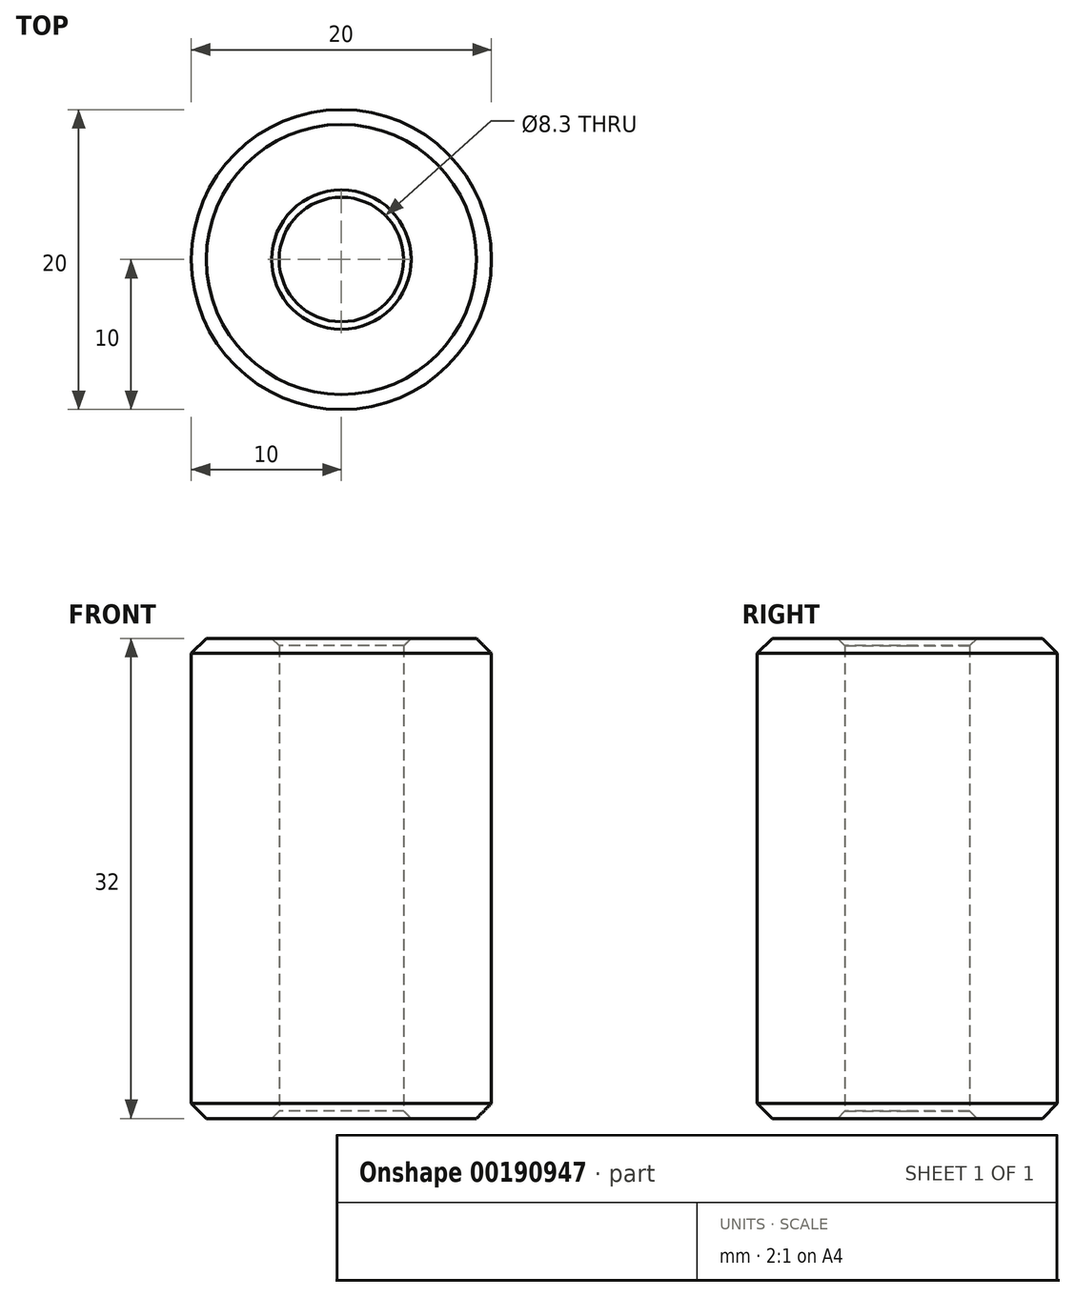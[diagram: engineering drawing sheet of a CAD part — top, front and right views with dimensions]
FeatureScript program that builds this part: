
annotation { "Feature Type Name" : "Feature", "Feature Type Description" : "" }
export const myFeature = defineFeature(function(context is Context, id is Id, definition is map)
    precondition{}
    {
        {
            var Q0;
            Q0=qCreatedBy(makeId("Top.planeOp"),FACE);
            var sketch = newSketch(context, id + "F0", { "sketchPlane" : qUnion([Q0])});
            skCircle(sketch, "E0", {"center": v(0, 0) * mm, "radius": 10 * mm});
            skCircle(sketch, "E1", {"center": v(0, 0) * mm, "radius": 4.15 * mm});
            skSolve(sketch);
        }
        {
            var Q0;
            Q0=makeQuery(id+"F0.imprint","IMPRINT",FACE,{"disambiguationData":[TD([[makeQuery(id+"F0.imprint","IMPRINT",EDGE,{"derivedFrom":sQuery(id+"F0.wireOp",EDGE,"E0")}),1.0]])]});
            extrude(context, id + "F1", {"entities" : qUnion([Q0]), "depth" : 32 * mm});
        }
        {
            var Q0;
            Q0=makeQuery(id+"F1.opExtrude","CAP_EDGE",EDGE,{"disambiguationData":[OSD([sQuery(id+"F0.wireOp",EDGE,"E0")])],"isStart":false});
            var Q1;
            Q1=makeQuery(id+"F1.opExtrude","SWEPT_FACE",FACE,{"disambiguationData":[OSD([sQuery(id+"F0.wireOp",EDGE,"E0")])]});
            chamfer(context, id + "F2", {"entities" : qUnion([Q0, Q1]), "width" : 1 * mm, "tangentPropagation" : true});
        }
        {
            var Q0;
            Q0=makeQuery(id+"F1.opExtrude","SWEPT_FACE",FACE,{"disambiguationData":[OSD([sQuery(id+"F0.wireOp",EDGE,"E1")])]});
            chamfer(context, id + "F3", {"entities" : qUnion([Q0]), "width" : 0.5 * mm, "tangentPropagation" : true});
        }
    });
